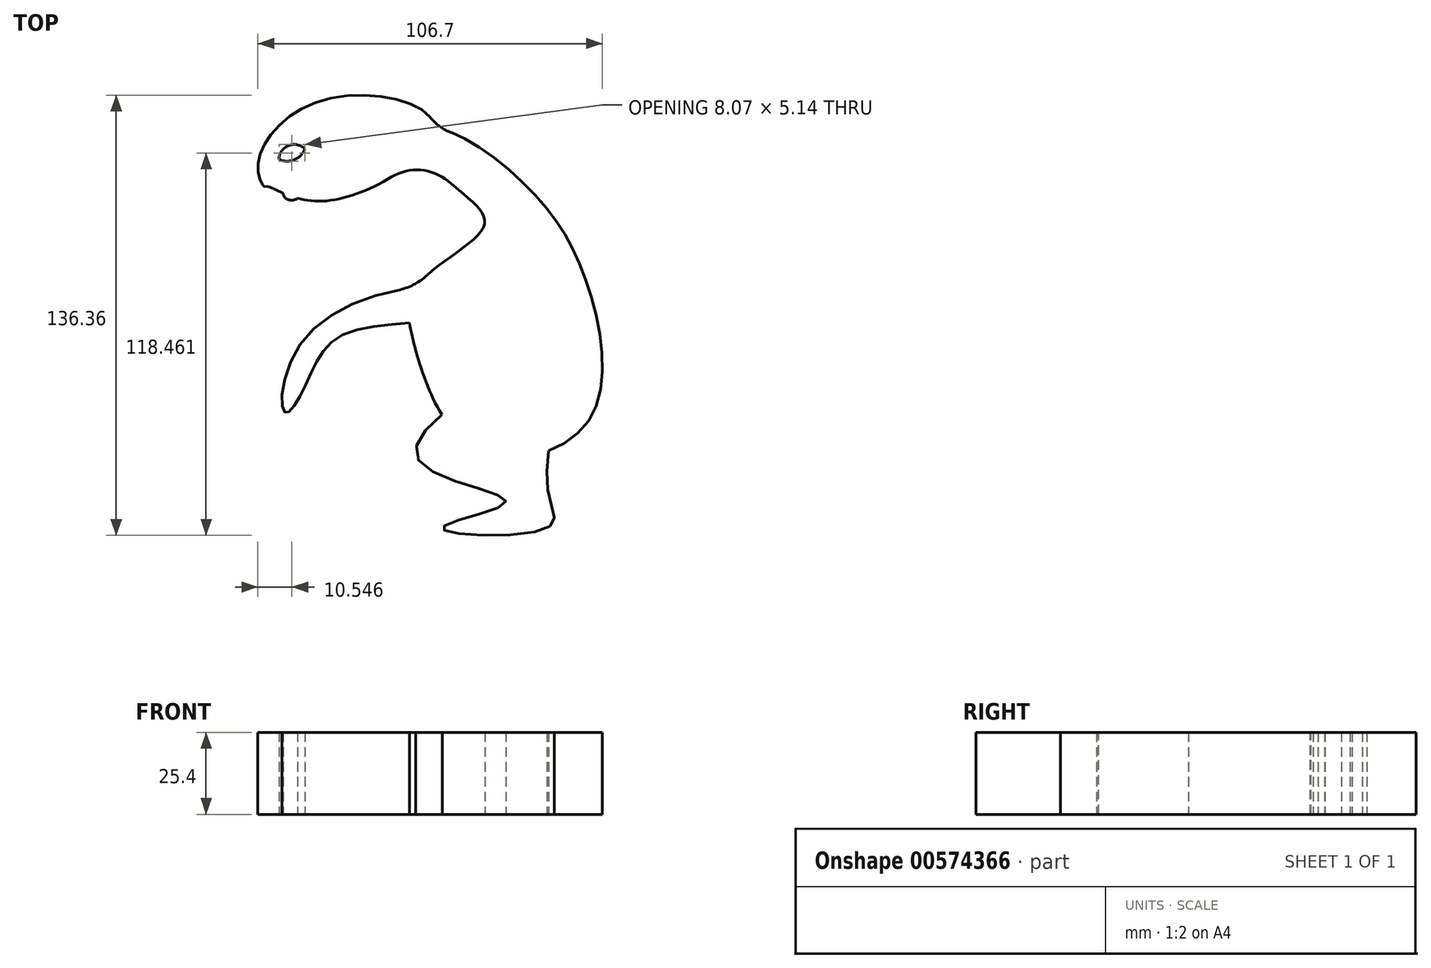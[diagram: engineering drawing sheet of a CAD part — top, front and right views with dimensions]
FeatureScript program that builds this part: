
annotation { "Feature Type Name" : "Feature", "Feature Type Description" : "" }
export const myFeature = defineFeature(function(context is Context, id is Id, definition is map)
    precondition{}
    {
        {
            var Q0;
            Q0=qCreatedBy(makeId("Top.planeOp"),FACE);
            var sketch = newSketch(context, id + "F0", { "sketchPlane" : qUnion([Q0])});
            skFitSpline(sketch, "E0", {"points": [v(-89.69, 15.8) * mm, v(-68.4, 35.8) * mm, v(-35.17, 27.1) * mm, v(-69.36, 4.2) * mm, v(-86.79, 8.7) * mm, v(-87.75, 8.7) * mm, v(-89.69, 15.8) * mm]});
            skArc(sketch, "E1", {"start": v(-75.17, 20.32) * mm, "mid": v(-80.26, 21.36) * mm, "end": v(-83.24, 17.1) * mm});
            skArc(sketch, "E2", {"start": v(-83.24, 17.1) * mm, "mid": v(-78.5, 16.97) * mm, "end": v(-75.17, 20.32) * mm});
            skFitSpline(sketch, "E3", {"points": [v(-81.93, 6.61) * mm, v(-75.17, 13.23) * mm, v(-77.46, 5.03) * mm, v(-81.93, 6.61) * mm]});
            skFitSpline(sketch, "E4", {"points": [v(-38.56, 19.54) * mm, v(-23.87, 4.51) * mm, v(-20, -4.2) * mm, v(-40, -21.62) * mm, v(-40.97, -41.62) * mm, v(-21.94, -72.6) * mm, v(11.94, -64.85) * mm, v(12.58, -22.59) * mm, v(-7.1, 9.35) * mm, v(-35.17, 26.1) * mm, v(-38.56, 19.54) * mm]});
            skFitSpline(sketch, "E5", {"points": [v(-27.75, -24.2) * mm, v(-73.23, -36.14) * mm, v(-81.3, -61.3) * mm, v(-75.17, -53.23) * mm, v(-63.23, -37.1) * mm, v(-30, -30.65) * mm, v(-27.75, -24.2) * mm]});
            skFitSpline(sketch, "E6", {"points": [v(-17.7, -53.53) * mm, v(-39.95, -76.17) * mm, v(-13.01, -89.05) * mm, v(-32.65, -97) * mm, v(0, -97) * mm, v(0, -85.31) * mm, v(0, -56.32) * mm, v(-17.7, -53.53) * mm]});
            skSolve(sketch);
        }
        {
            var Q0;
            Q0 = qSketchRegion(id + "F0", true);
            extrude(context, id + "F1", {"entities" : qUnion([Q0]), "depth" : 25.4 * mm, "offsetDistance" : 25.4 * mm});
        }
        {
            var Q0;
            {var subQ0=sQuery(id+"F0.wireOp",EDGE,"E4");var subQ1=sQuery(id+"F0.wireOp",EDGE,"E0");Q0=makeQuery(id+"F1.opExtrude","SWEPT_EDGE",EDGE,{"disambiguationData":[OSD([subQ1,subQ0]),TDD([makeQuery(id+"F0.imprint","INTERSECT",VERTEX,{"disambiguationData":[OD(0.0)],"derivedFrom":[subQ1,subQ0]})])]});}
            var Q1;
            {var subQ0=sQuery(id+"F0.wireOp",EDGE,"E4");var subQ1=sQuery(id+"F0.wireOp",EDGE,"E0");Q1=makeQuery(id+"F1.opExtrude","SWEPT_EDGE",EDGE,{"disambiguationData":[OSD([subQ1,subQ0]),TDD([makeQuery(id+"F0.imprint","INTERSECT",VERTEX,{"disambiguationData":[OD(1.0)],"derivedFrom":[subQ1,subQ0]})])]});}
            fillet(context, id + "F2", {"entities" : qUnion([Q0, Q1]), "radius" : 15.1 * mm, "tangentPropagation" : true, "allowEdgeOverflow" : false});
        }
        {
            var Q0;
            {var subQ0=sQuery(id+"F0.wireOp",EDGE,"E5");var subQ1=sQuery(id+"F0.wireOp",EDGE,"E4");Q0=makeQuery(id+"F1.opExtrude","SWEPT_EDGE",EDGE,{"disambiguationData":[OSD([subQ1,subQ0]),TDD([makeQuery(id+"F0.imprint","INTERSECT",VERTEX,{"disambiguationData":[OD(0.0)],"derivedFrom":[subQ1,subQ0]})])]});}
            fillet(context, id + "F3", {"entities" : qUnion([Q0]), "radius" : 18.73 * mm, "tangentPropagation" : true, "allowEdgeOverflow" : false});
        }
    });
